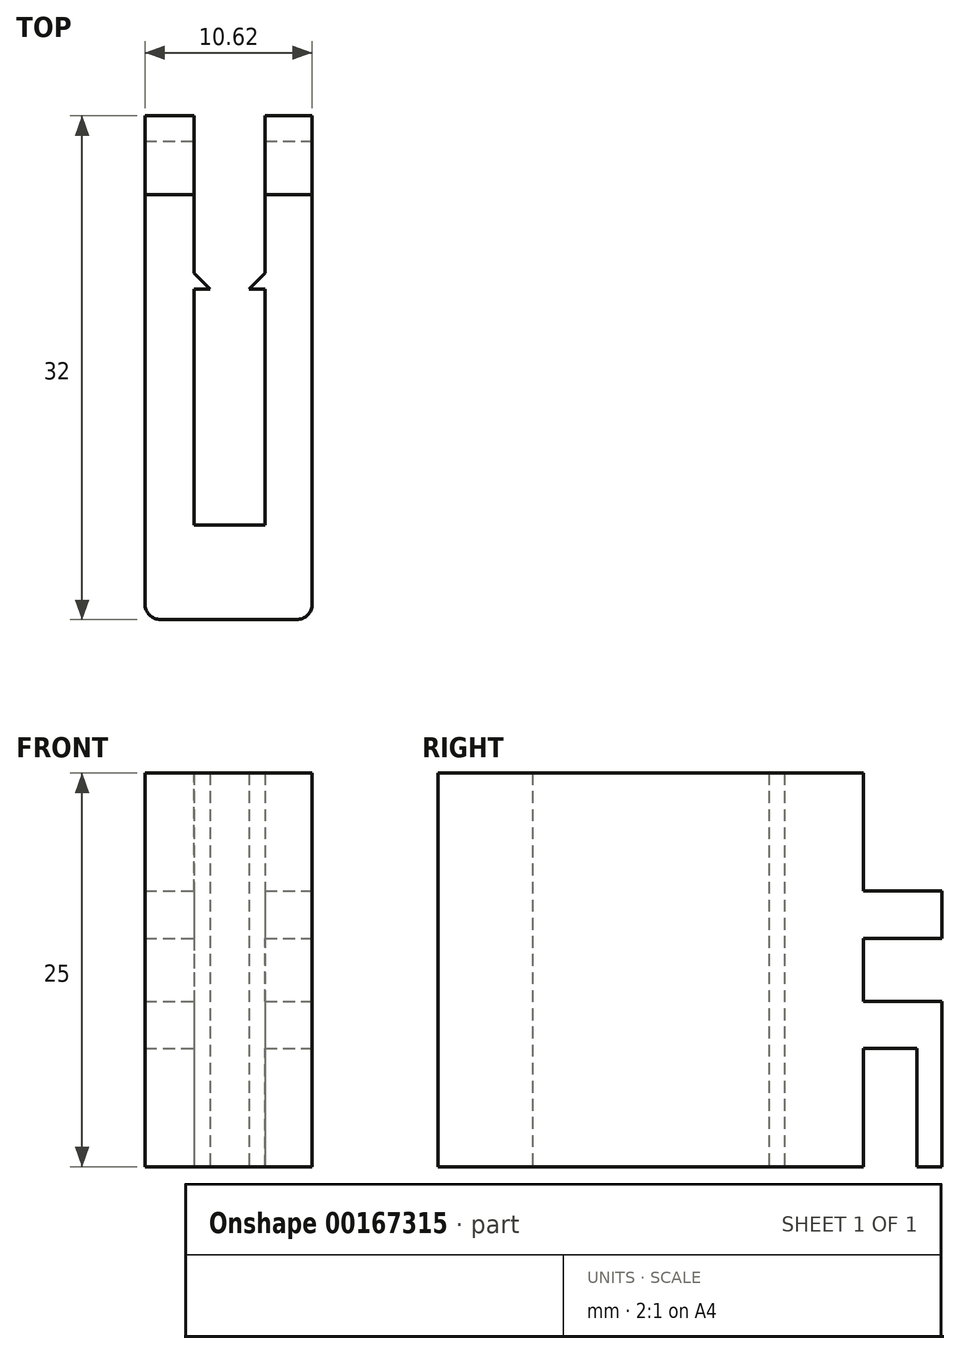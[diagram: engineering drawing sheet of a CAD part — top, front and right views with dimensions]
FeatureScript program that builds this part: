
annotation { "Feature Type Name" : "Feature", "Feature Type Description" : "" }
export const myFeature = defineFeature(function(context is Context, id is Id, definition is map)
    precondition{}
    {
        {
            var Q0;
            Q0=qCreatedBy(makeId("Top.planeOp"),FACE);
            var sketch = newSketch(context, id + "F0", { "sketchPlane" : qUnion([Q0])});
            skLineSegment(sketch, "E0", {"start": v(0, 0) * mm, "end": v(0, 15) * mm});
            skLineSegment(sketch, "E1", {"start": v(0, 0) * mm, "end": v(4.5, 0) * mm});
            skLineSegment(sketch, "E2", {"start": v(4.5, 0) * mm, "end": v(4.5, 15) * mm});
            skLineSegment(sketch, "E3", {"start": v(-3.12, 15) * mm, "end": v(-3.12, 0) * mm});
            skLineSegment(sketch, "E4", {"start": v(-3.12, 0) * mm, "end": v(-3.12, -5) * mm});
            skLineSegment(sketch, "E5", {"start": v(-2.12, -6) * mm, "end": v(4.5, -6) * mm});
            skLineSegment(sketch, "E6", {"start": v(4.5, -6) * mm, "end": v(6.5, -6) * mm});
            skLineSegment(sketch, "E7", {"start": v(7.5, -5) * mm, "end": v(7.5, 15) * mm});
            skLineSegment(sketch, "E8", {"start": v(-3.12, 15) * mm, "end": v(-3.12, 16) * mm});
            skLineSegment(sketch, "E9", {"start": v(-3.12, 16) * mm, "end": v(0, 16) * mm});
            skLineSegment(sketch, "E10", {"start": v(4.5, 16) * mm, "end": v(7.5, 16) * mm});
            skLineSegment(sketch, "E11", {"start": v(7.5, 16) * mm, "end": v(7.5, 15) * mm});
            skLineSegment(sketch, "E12", {"start": v(1, 15) * mm, "end": v(0, 15) * mm});
            skLineSegment(sketch, "E13", {"start": v(3.5, 15) * mm, "end": v(4.5, 15) * mm});
            skPoint(sketch, "E14.visualSharp", {"position": v(-3.12, -6) * mm});
            skArc(sketch, "E14.filletArc", {"start": v(-3.12, -5) * mm, "mid": v(-2.83, -5.7) * mm, "end": v(-2.12, -6) * mm});
            skPoint(sketch, "E15.visualSharp", {"position": v(7.5, -6) * mm});
            skArc(sketch, "E15.filletArc", {"start": v(6.5, -6) * mm, "mid": v(7.2, -5.7) * mm, "end": v(7.5, -5) * mm});
            skLineSegment(sketch, "E16", {"start": v(-3.12, 16) * mm, "end": v(-3.12, 26) * mm});
            skLineSegment(sketch, "E17", {"start": v(-3.12, 26) * mm, "end": v(0, 26) * mm});
            skLineSegment(sketch, "E18", {"start": v(0, 26) * mm, "end": v(0, 16) * mm});
            skLineSegment(sketch, "E19", {"start": v(4.5, 16) * mm, "end": v(4.5, 26) * mm});
            skLineSegment(sketch, "E20", {"start": v(7.5, 16) * mm, "end": v(7.5, 26) * mm});
            skLineSegment(sketch, "E21", {"start": v(7.5, 26) * mm, "end": v(4.5, 26) * mm});
            skLineSegment(sketch, "E22", {"start": v(1, 15) * mm, "end": v(0, 16) * mm});
            skLineSegment(sketch, "E23", {"start": v(3.5, 15) * mm, "end": v(4.5, 16) * mm});
            skSolve(sketch);
        }
        {
            var Q0;
            Q0=makeQuery(id+"F0.imprint","IMPRINT",FACE,{"disambiguationData":[TD([[makeQuery(id+"F0.imprint","IMPRINT",EDGE,{"derivedFrom":sQuery(id+"F0.wireOp",EDGE,"E0")}),1.0]])]});
            extrude(context, id + "F1", {"entities" : qUnion([Q0]), "depth" : 25 * mm});
        }
        {
            var Q0;
            Q0 = qSketchRegion(id + "F0", true);
            extrude(context, id + "F2", {"entities" : qUnion([Q0]), "operationType" : NewBodyOperationType.ADD, "depth" : 25 * mm});
        }
        {
            var Q0;
            {var subQ0=sQuery(id+"F0.wireOp",EDGE,"E11");var subQ1=sQuery(id+"F0.wireOp",EDGE,"E7");Q0=makeQuery(id+"F2.boolean.opBoolean","MERGE",FACE,{"derivedFrom":[makeQuery(id+"F1.opExtrude","SWEPT_FACE",FACE,{"disambiguationData":[OSD([subQ1,subQ0])]}),makeQuery(id+"F2.opExtrude","SWEPT_FACE",FACE,{"disambiguationData":[OSD([subQ1,subQ0,sQuery(id+"F0.wireOp",EDGE,"E20")])]})]});}
            var sketch = newSketch(context, id + "F3", { "sketchPlane" : qUnion([Q0])});
            skLineSegment(sketch, "E24", {"start": v(26, 25) * mm, "end": v(26, 3) * mm});
            skLineSegment(sketch, "E25", {"start": v(26, 25) * mm, "end": v(26, 12.5) * mm});
            skLineSegment(sketch, "E26", {"start": v(26, 12.5) * mm, "end": v(26, 14) * mm});
            skLineSegment(sketch, "E27", {"start": v(26, 11) * mm, "end": v(26, 14) * mm});
            skLineSegment(sketch, "E28", {"start": v(26, 12.5) * mm, "end": v(26, 14.5) * mm});
            skLineSegment(sketch, "E29", {"start": v(26, 14.5) * mm, "end": v(21, 14.5) * mm});
            skLineSegment(sketch, "E30", {"start": v(21, 14.5) * mm, "end": v(21, 10.5) * mm});
            skLineSegment(sketch, "E31", {"start": v(21, 10.5) * mm, "end": v(26, 10.5) * mm});
            skLineSegment(sketch, "E32.bottom", {"start": v(26, 10.5) * mm, "end": v(24.4, 10.5) * mm});
            skLineSegment(sketch, "E32.top", {"start": v(26, 14.5) * mm, "end": v(24.4, 14.5) * mm});
            skLineSegment(sketch, "E32.left", {"start": v(26, 10.5) * mm, "end": v(26, 14.5) * mm});
            skLineSegment(sketch, "E32.right", {"start": v(24.4, 10.5) * mm, "end": v(24.4, 14.5) * mm});
            skLineSegment(sketch, "E33", {"start": v(21, 14.5) * mm, "end": v(21, 17.5) * mm});
            skLineSegment(sketch, "E34", {"start": v(21, 10.5) * mm, "end": v(21, 7.5) * mm});
            skLineSegment(sketch, "E35.bottom", {"start": v(24.4, 7.5) * mm, "end": v(21, 7.5) * mm});
            skLineSegment(sketch, "E35.top", {"start": v(24.4, 0) * mm, "end": v(21, 0) * mm});
            skLineSegment(sketch, "E35.left", {"start": v(24.4, 7.5) * mm, "end": v(24.4, 0) * mm});
            skLineSegment(sketch, "E35.right", {"start": v(21, 7.5) * mm, "end": v(21, 0) * mm});
            skLineSegment(sketch, "E36.bottom", {"start": v(21, 17.5) * mm, "end": v(26, 17.5) * mm});
            skLineSegment(sketch, "E36.top", {"start": v(21, 25) * mm, "end": v(26, 25) * mm});
            skLineSegment(sketch, "E36.left", {"start": v(21, 17.5) * mm, "end": v(21, 25) * mm});
            skLineSegment(sketch, "E36.right", {"start": v(26, 17.5) * mm, "end": v(26, 25) * mm});
            skSolve(sketch);
        }
        {
            var Q0;
            Q0=makeQuery(id+"F3.imprint","IMPRINT",FACE,{"disambiguationData":[TD([[makeQuery(id+"F3.imprint","IMPRINT",EDGE,{"derivedFrom":sQuery(id+"F3.wireOp",EDGE,"E29")}),1.0]])]});
            var Q1;
            Q1=makeQuery(id+"F3.imprint","IMPRINT",FACE,{"disambiguationData":[TD([[makeQuery(id+"F3.imprint","IMPRINT",EDGE,{"derivedFrom":sQuery(id+"F3.wireOp",EDGE,"t2AucNpj-j5sO-Vg8m-oUTu-52qLNZS0L9KU.bottom")}),1.0]])]});
            var Q2;
            Q2=makeQuery(id+"F3.imprint","IMPRINT",FACE,{"disambiguationData":[TD([[makeQuery(id+"F3.imprint","IMPRINT",EDGE,{"derivedFrom":sQuery(id+"F3.wireOp",EDGE,"RXK6u0mf-v7J3-dM4o-qh1P-WhWb1DFgNDoP.bottom")}),1.0]])]});
            var Q3;
            Q3=makeQuery(id+"F3.imprint","IMPRINT",FACE,{"disambiguationData":[TD([[makeQuery(id+"F3.imprint","IMPRINT",EDGE,{"derivedFrom":sQuery(id+"F3.wireOp",EDGE,"E36.bottom")}),1.0]])]});
            var Q4;
            Q4=makeQuery(id+"F3.imprint","IMPRINT",FACE,{"disambiguationData":[TD([[makeQuery(id+"F3.imprint","IMPRINT",EDGE,{"derivedFrom":sQuery(id+"F3.wireOp",EDGE,"E35.bottom")}),1.0]])]});
            extrude(context, id + "F4", {"entities" : qUnion([Q0, Q1, Q2, Q3, Q4]), "operationType" : NewBodyOperationType.REMOVE, "oppositeDirection" : true, "depth" : 25 * mm});
        }
    });
